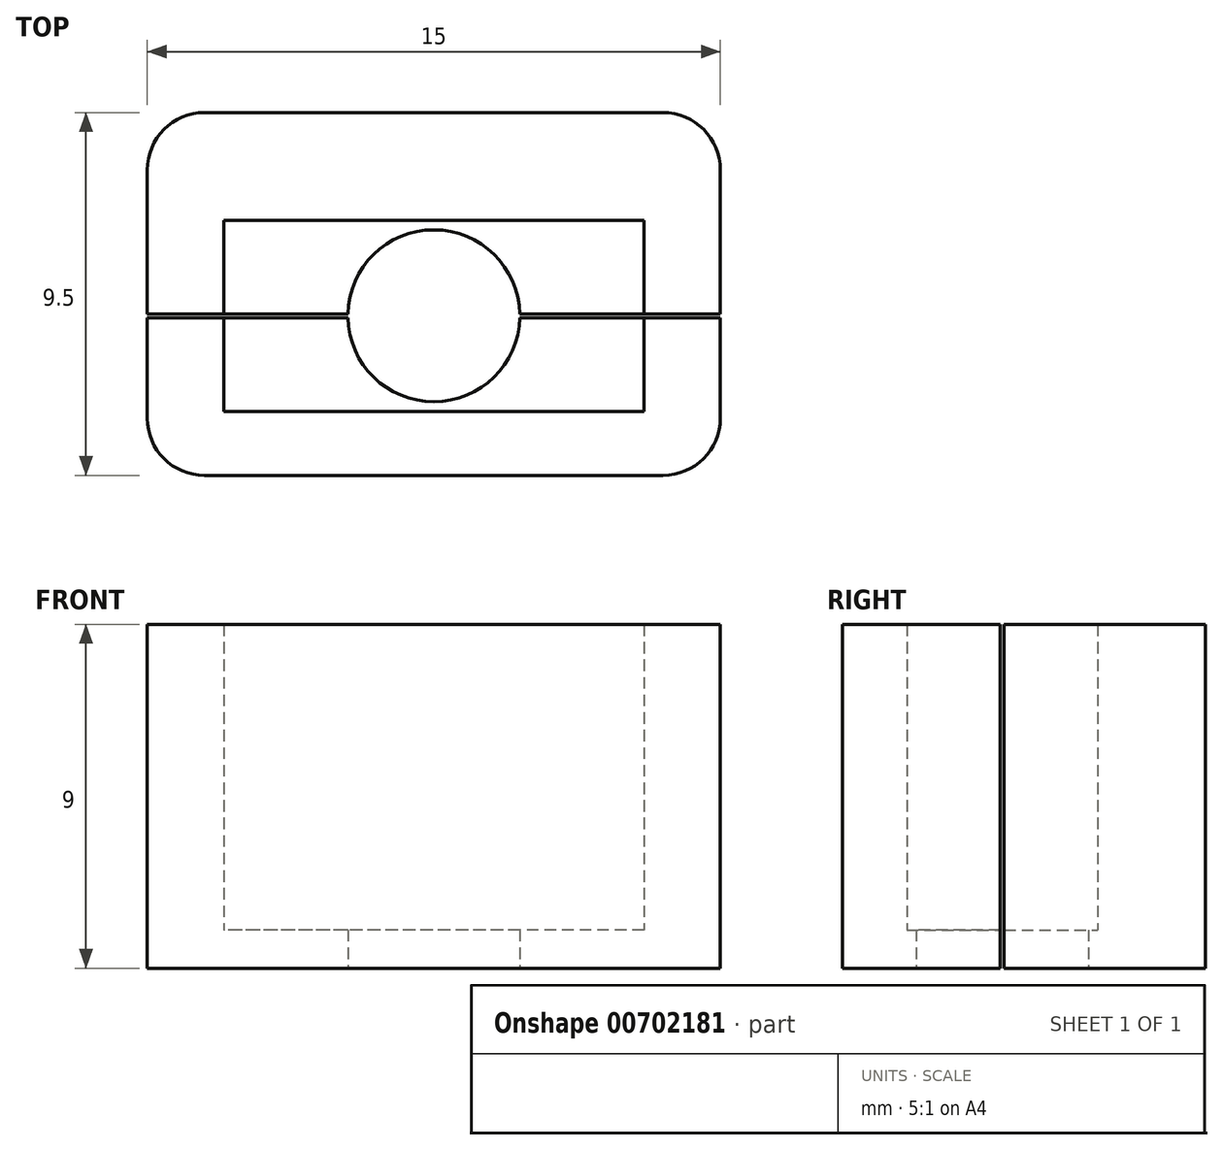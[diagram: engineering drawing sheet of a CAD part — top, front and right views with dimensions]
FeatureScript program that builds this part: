
annotation { "Feature Type Name" : "Feature", "Feature Type Description" : "" }
export const myFeature = defineFeature(function(context is Context, id is Id, definition is map)
    precondition{}
    {
        {
            var Q0;
            Q0=qCreatedBy(makeId("Top.planeOp"),FACE);
            var sketch = newSketch(context, id + "F0", { "sketchPlane" : qUnion([Q0])});
            skPoint(sketch, "E0.middle", {"position": v(0, 0) * mm});
            skPoint(sketch, "E1.middle", {"position": v(0, 3.26) * mm});
            skPoint(sketch, "E1.middle.positionSnap0", {"position": v(0, 2.5) * mm});
            skPoint(sketch, "E1.centerSnap0", {"position": v(0, 2.5) * mm});
            skLineSegment(sketch, "E2.bottom", {"start": v(7.5, -4.18) * mm, "end": v(-7.5, -4.18) * mm});
            skLineSegment(sketch, "E2.top", {"start": v(7.5, 5.32) * mm, "end": v(-7.5, 5.32) * mm});
            skLineSegment(sketch, "E2.left", {"start": v(7.5, -4.18) * mm, "end": v(7.5, 5.32) * mm});
            skLineSegment(sketch, "E2.right", {"start": v(-7.5, -4.18) * mm, "end": v(-7.5, 5.32) * mm});
            skPoint(sketch, "E2.middle", {"position": v(0, 0.57) * mm});
            skLineSegment(sketch, "E3.bottom", {"start": v(5.5, -2.5) * mm, "end": v(-5.5, -2.5) * mm});
            skLineSegment(sketch, "E3.top", {"start": v(5.5, 2.5) * mm, "end": v(-5.5, 2.5) * mm});
            skLineSegment(sketch, "E3.left", {"start": v(5.5, -2.5) * mm, "end": v(5.5, 2.5) * mm});
            skLineSegment(sketch, "E3.right", {"start": v(-5.5, -2.5) * mm, "end": v(-5.5, 2.5) * mm});
            skCircle(sketch, "E4", {"center": v(0, 0) * mm, "radius": 2.25 * mm});
            skSolve(sketch);
        }
        {
            var Q0;
            Q0=makeQuery(id+"F0.imprint","IMPRINT",FACE,{"disambiguationData":[TD([[makeQuery(id+"F0.imprint","IMPRINT",EDGE,{"derivedFrom":sQuery(id+"F0.wireOp",EDGE,"tryETO4A-KLSB-25rD-V5az-C2slfdcLXtNE.bottom")}),1.0]])]});
            var Q1;
            Q1=makeQuery(id+"F0.imprint","IMPRINT",FACE,{"disambiguationData":[TD([[makeQuery(id+"F0.imprint","IMPRINT",EDGE,{"derivedFrom":sQuery(id+"F0.wireOp",EDGE,"E2.bottom")}),-1.0]])]});
            extrude(context, id + "F1", {"entities" : qUnion([Q0, Q1]), "depth" : 9 * mm, "offsetDistance" : 25 * mm});
        }
        {
            var Q0;
            Q0=makeQuery(id+"F1.opExtrude","SWEPT_EDGE",EDGE,{"disambiguationData":[OSD([sQuery(id+"F0.wireOp",EDGE,"E2.top"),sQuery(id+"F0.wireOp",EDGE,"E2.right")])]});
            var Q1;
            Q1=makeQuery(id+"F1.opExtrude","SWEPT_EDGE",EDGE,{"disambiguationData":[OSD([sQuery(id+"F0.wireOp",EDGE,"E2.top"),sQuery(id+"F0.wireOp",EDGE,"E2.left")])]});
            var Q2;
            Q2=makeQuery(id+"F1.opExtrude","SWEPT_EDGE",EDGE,{"disambiguationData":[OSD([sQuery(id+"F0.wireOp",EDGE,"E2.bottom"),sQuery(id+"F0.wireOp",EDGE,"E2.left")])]});
            var Q3;
            Q3=makeQuery(id+"F1.opExtrude","SWEPT_EDGE",EDGE,{"disambiguationData":[OSD([sQuery(id+"F0.wireOp",EDGE,"E2.bottom"),sQuery(id+"F0.wireOp",EDGE,"E2.right")])]});
            fillet(context, id + "F2", {"entities" : qUnion([Q0, Q1, Q2, Q3]), "radius" : 1.5 * mm, "tangentPropagation" : true, "allowEdgeOverflow" : false});
        }
        {
            var Q0;
            Q0=makeQuery(id+"F0.imprint","IMPRINT",FACE,{"disambiguationData":[TD([[makeQuery(id+"F0.imprint","IMPRINT",EDGE,{"derivedFrom":sQuery(id+"F0.wireOp",EDGE,"E3.bottom")}),-1.0]])]});
            extrude(context, id + "F3", {"entities" : qUnion([Q0]), "operationType" : NewBodyOperationType.ADD, "depth" : 1 * mm, "offsetDistance" : 25 * mm});
        }
        {
            var Q0;
            Q0=makeQuery(id+"F1.opExtrude","CAP_FACE",FACE,{"disambiguationData":[OSD([sQuery(id+"F0.wireOp",EDGE,"E2.bottom"),sQuery(id+"F0.wireOp",EDGE,"E2.top"),sQuery(id+"F0.wireOp",EDGE,"E2.left"),sQuery(id+"F0.wireOp",EDGE,"E2.right"),sQuery(id+"F0.wireOp",EDGE,"E3.bottom"),sQuery(id+"F0.wireOp",EDGE,"E3.top"),sQuery(id+"F0.wireOp",EDGE,"E3.left"),sQuery(id+"F0.wireOp",EDGE,"E3.right")])],"isStart":false});
            var sketch = newSketch(context, id + "F4", { "sketchPlane" : qUnion([Q0])});
            skLineSegment(sketch, "E5.bottom", {"start": v(14.7, -0.05) * mm, "end": v(-14.7, -0.05) * mm});
            skLineSegment(sketch, "E5.top", {"start": v(14.7, 0.05) * mm, "end": v(-14.7, 0.05) * mm});
            skLineSegment(sketch, "E5.left", {"start": v(14.7, -0.05) * mm, "end": v(14.7, 0.05) * mm});
            skLineSegment(sketch, "E5.right", {"start": v(-14.7, -0.05) * mm, "end": v(-14.7, 0.05) * mm});
            skPoint(sketch, "E5.middle", {"position": v(0, 0) * mm});
            skSolve(sketch);
        }
        {
            var Q0;
            {var subQ0=sQuery(id+"F4.wireOp",EDGE,"E5.bottom");var subQ1=makeQuery(id+"F1.opExtrude","CAP_EDGE",EDGE,{"disambiguationData":[OSD([sQuery(id+"F0.wireOp",EDGE,"E2.right")])],"isStart":false});var subQ2=makeQuery(id+"F4.imprint","INTERSECT",VERTEX,{"derivedFrom":[subQ1,subQ0]});Q0=makeQuery(id+"F4.imprint","IMPRINT",FACE,{"disambiguationData":[TD([[makeQuery(id+"F4.imprint","IMPRINT",EDGE,{"disambiguationData":[TD([[subQ2,1.0]])],"derivedFrom":subQ0}),-1.0]])]});}
            var Q1;
            {var subQ0=sQuery(id+"F4.wireOp",EDGE,"E5.bottom");var subQ1=makeQuery(id+"F1.opExtrude","CAP_EDGE",EDGE,{"disambiguationData":[OSD([sQuery(id+"F0.wireOp",EDGE,"E3.left")])],"isStart":false});var subQ2=makeQuery(id+"F4.imprint","INTERSECT",VERTEX,{"derivedFrom":[subQ1,subQ0]});Q1=makeQuery(id+"F4.imprint","IMPRINT",FACE,{"disambiguationData":[TD([[makeQuery(id+"F4.imprint","IMPRINT",EDGE,{"disambiguationData":[TD([[subQ2,-1.0]])],"derivedFrom":subQ0}),-1.0]])]});}
            var Q2;
            {var subQ0=sQuery(id+"F4.wireOp",EDGE,"E5.bottom");var subQ1=makeQuery(id+"F1.opExtrude","CAP_EDGE",EDGE,{"disambiguationData":[OSD([sQuery(id+"F0.wireOp",EDGE,"E2.left")])],"isStart":false});var subQ2=makeQuery(id+"F4.imprint","INTERSECT",VERTEX,{"derivedFrom":[subQ1,subQ0]});Q2=makeQuery(id+"F4.imprint","IMPRINT",FACE,{"disambiguationData":[TD([[makeQuery(id+"F4.imprint","IMPRINT",EDGE,{"disambiguationData":[TD([[subQ2,-1.0]])],"derivedFrom":subQ0}),-1.0]])]});}
            extrude(context, id + "F5", {"entities" : qUnion([Q0, Q1, Q2]), "operationType" : NewBodyOperationType.REMOVE, "oppositeDirection" : true, "depth" : 25 * mm, "offsetDistance" : 25 * mm});
        }
    });
